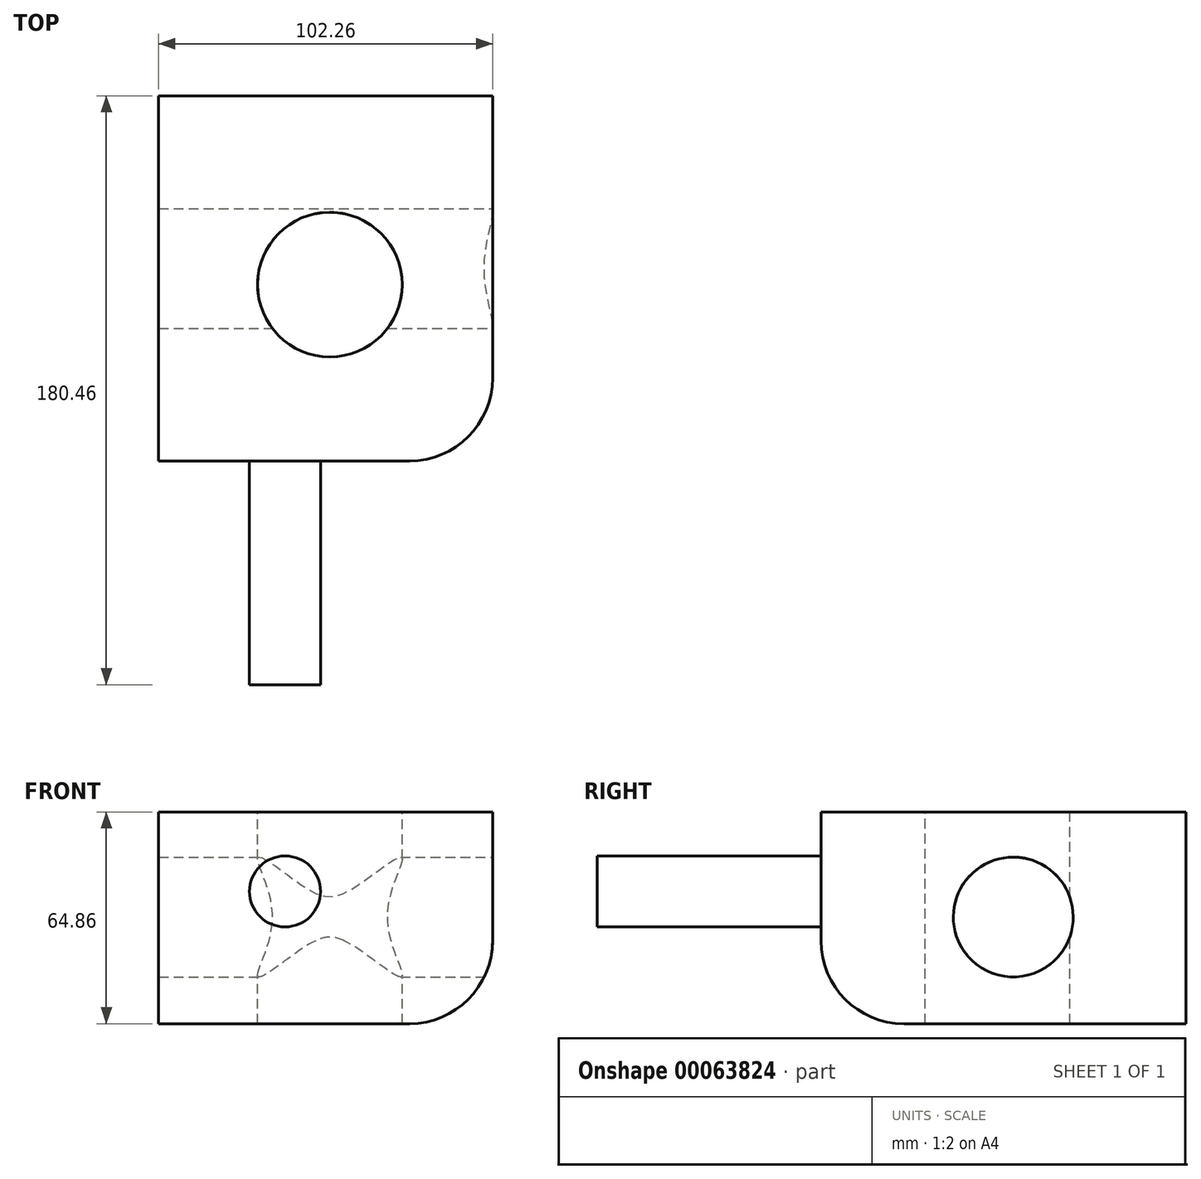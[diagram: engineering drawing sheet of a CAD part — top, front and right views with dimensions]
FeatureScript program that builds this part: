
annotation { "Feature Type Name" : "Feature", "Feature Type Description" : "" }
export const myFeature = defineFeature(function(context is Context, id is Id, definition is map)
    precondition{}
    {
        {
            var Q0;
            Q0=qCreatedBy(makeId("Front.planeOp"),FACE);
            var sketch = newSketch(context, id + "F0", { "sketchPlane" : qUnion([Q0])});
            skLineSegment(sketch, "E0.bottom", {"start": v(0, 0) * mm, "end": v(102.26, 0) * mm});
            skLineSegment(sketch, "E0.top", {"start": v(0, 64.86) * mm, "end": v(102.26, 64.86) * mm});
            skLineSegment(sketch, "E0.left", {"start": v(0, 0) * mm, "end": v(0, 64.86) * mm});
            skLineSegment(sketch, "E0.right", {"start": v(102.26, 0) * mm, "end": v(102.26, 64.86) * mm});
            skSolve(sketch);
        }
        {
            var Q0;
            Q0=makeQuery(id+"F0.imprint","IMPRINT",FACE,{"disambiguationData":[TD([[makeQuery(id+"F0.imprint","IMPRINT",EDGE,{"derivedFrom":sQuery(id+"F0.wireOp",EDGE,"E0.bottom")}),1.0]])]});
            extrude(context, id + "F1", {"entities" : qUnion([Q0]), "depth" : 111.87 * mm});
        }
        {
            var Q0;
            Q0=makeQuery(id+"F1.opExtrude","SWEPT_FACE",FACE,{"disambiguationData":[OSD([sQuery(id+"F0.wireOp",EDGE,"E0.top")])]});
            var sketch = newSketch(context, id + "F2", { "sketchPlane" : qUnion([Q0])});
            skCircle(sketch, "E1", {"center": v(52.44, -57.84) * mm, "radius": 22.16 * mm});
            skSolve(sketch);
        }
        {
            var Q0;
            Q0 = qSketchRegion(id + "F2", true);
            extrude(context, id + "F3", {"entities" : qUnion([Q0]), "operationType" : NewBodyOperationType.REMOVE, "oppositeDirection" : true, "depth" : 123.48 * mm});
        }
        {
            var Q0;
            Q0=makeQuery(id+"F1.opExtrude","SWEPT_FACE",FACE,{"disambiguationData":[OSD([sQuery(id+"F0.wireOp",EDGE,"E0.right")])]});
            var sketch = newSketch(context, id + "F4", { "sketchPlane" : qUnion([Q0])});
            skCircle(sketch, "E2", {"center": v(-52.96, 32.7) * mm, "radius": 18.35 * mm});
            skSolve(sketch);
        }
        {
            var Q0;
            Q0 = qSketchRegion(id + "F4", true);
            extrude(context, id + "F5", {"entities" : qUnion([Q0]), "operationType" : NewBodyOperationType.REMOVE, "oppositeDirection" : true, "depth" : 205.67 * mm});
        }
        {
            var Q0;
            Q0=makeQuery(id+"F1.opExtrude","CAP_EDGE",EDGE,{"disambiguationData":[OSD([sQuery(id+"F0.wireOp",EDGE,"E0.bottom")])],"isStart":false});
            var Q1;
            Q1=makeQuery(id+"F1.opExtrude","CAP_EDGE",EDGE,{"disambiguationData":[OSD([sQuery(id+"F0.wireOp",EDGE,"E0.right")])],"isStart":false});
            var Q2;
            Q2=makeQuery(id+"F1.opExtrude","SWEPT_EDGE",EDGE,{"disambiguationData":[OSD([sQuery(id+"F0.wireOp",EDGE,"E0.bottom"),sQuery(id+"F0.wireOp",EDGE,"E0.right")])]});
            fillet(context, id + "F6", {"entities" : qUnion([Q0, Q1, Q2]), "radius" : 25.4 * mm, "tangentPropagation" : true, "allowEdgeOverflow" : false});
        }
        {
            var Q0;
            Q0=makeQuery(id+"F1.opExtrude","CAP_FACE",FACE,{"disambiguationData":[OSD([sQuery(id+"F0.wireOp",EDGE,"E0.bottom"),sQuery(id+"F0.wireOp",EDGE,"E0.top"),sQuery(id+"F0.wireOp",EDGE,"E0.left"),sQuery(id+"F0.wireOp",EDGE,"E0.right")])],"isStart":false});
            var sketch = newSketch(context, id + "F7", { "sketchPlane" : qUnion([Q0])});
            skCircle(sketch, "E3", {"center": v(38.7, 40.52) * mm, "radius": 10.88 * mm});
            skSolve(sketch);
        }
        {
            var Q0;
            Q0 = qSketchRegion(id + "F7", true);
            extrude(context, id + "F8", {"entities" : qUnion([Q0]), "operationType" : NewBodyOperationType.ADD, "depth" : 68.6 * mm});
        }
    });
